# Revit family: Domotics-DomesticRanges-GEWISS-27COMBIDIN_SYSTEM-IP40_8M_16SY
name_source: partatom
category: Apparecchi elettrici
revit_build: Autodesk Revit 2016 (Build: 20161004_0715(x64)
units: mm (PartAtom-declared; Revit-internal decimal feet)

## family parameters
Condiviso = No
Host = Superficie
Mantenere orientamento annotazione = No
Punto di calcolo locali = No
Quota connettore circolare = Usa diametro
Taglio con vuoti quando caricato = No
Tipo di parte = Normale

## types (1)
- Domotics-DomesticRanges-GEWISS-27COMBIDIN_SYSTEM-IP40_8M_16SY
    Altezza = 132 mm
    Catalogue = DOMOTICS
    Catalogue Range = 27COMBI
    Characteristics = Halogen free
    Colour = Grey RAL 7035
    Compartment pre-arrangement = 2
    Configuration = Module 4 x 4
    Descrizione = ENCLOSURE 8MOD.DIN+(4X4)MOD.SYSTEM
    Dispersible power (W) = 18
    Door colour: = Smoked Transparent
    Door type = Rigid
    EAN code = 8011564055469
    Electrocod = 0212
    Glow Wire Test = 650°C
    IDF = ce4d066f-44da-477c-8463-b113b2043b21
    IDT = 6c31ff9f-37c3-42df-829d-006412dd97ed
    IP degree = IP40
    Immagine tipo = GW27073.jpg
    Installation temperature = -25 +60 °C
    Insulation class = II
    Insulation voltage = 750V
    Larghezza = 429 mm  [stored 1.40748 ft]
    Lid screws = Stainless steel
    Modello = GW27073
    No. DIN modules = 8
    No. SYSTEM modules = 16
    No. knockout holes Ã˜ 23 = 18
    No. knockout holes Ã˜23 = 18 on sides / 2 on the bottom
    Outer dim. LxHxD (mm) = 429x132x95
    Produttore = GEWISS S.p.A.
    Profondità = 95 mm
    Prospetto di default = 1219 mm
    Rated current (In) = 32A
    Rated voltage: = 400V ac
    SEO = Enclosure
    Shock resistance = IK07
    Standard = EN 60669-2-1
    Standard; = EN 60670-1 - EN 60670-24
    Technical sheet = https://www.gewiss.com
    Thermo-pressure with ball = 70
    Torque screws tightening = 0,8NM
    Type of enclosure = GP
    Type of knockout holes = Removable with tool
    URL = https://www.gewiss.com
    Version file RFA = 19.4

note: source unit labels omitted for Thermo-pressure with ball — the stored unit's dimension contradicts the parameter name (converter mislabeling)

note: [stored X ft] marks values corroborated as IEEE doubles in the binary element streams (Revit-internal decimal feet)
